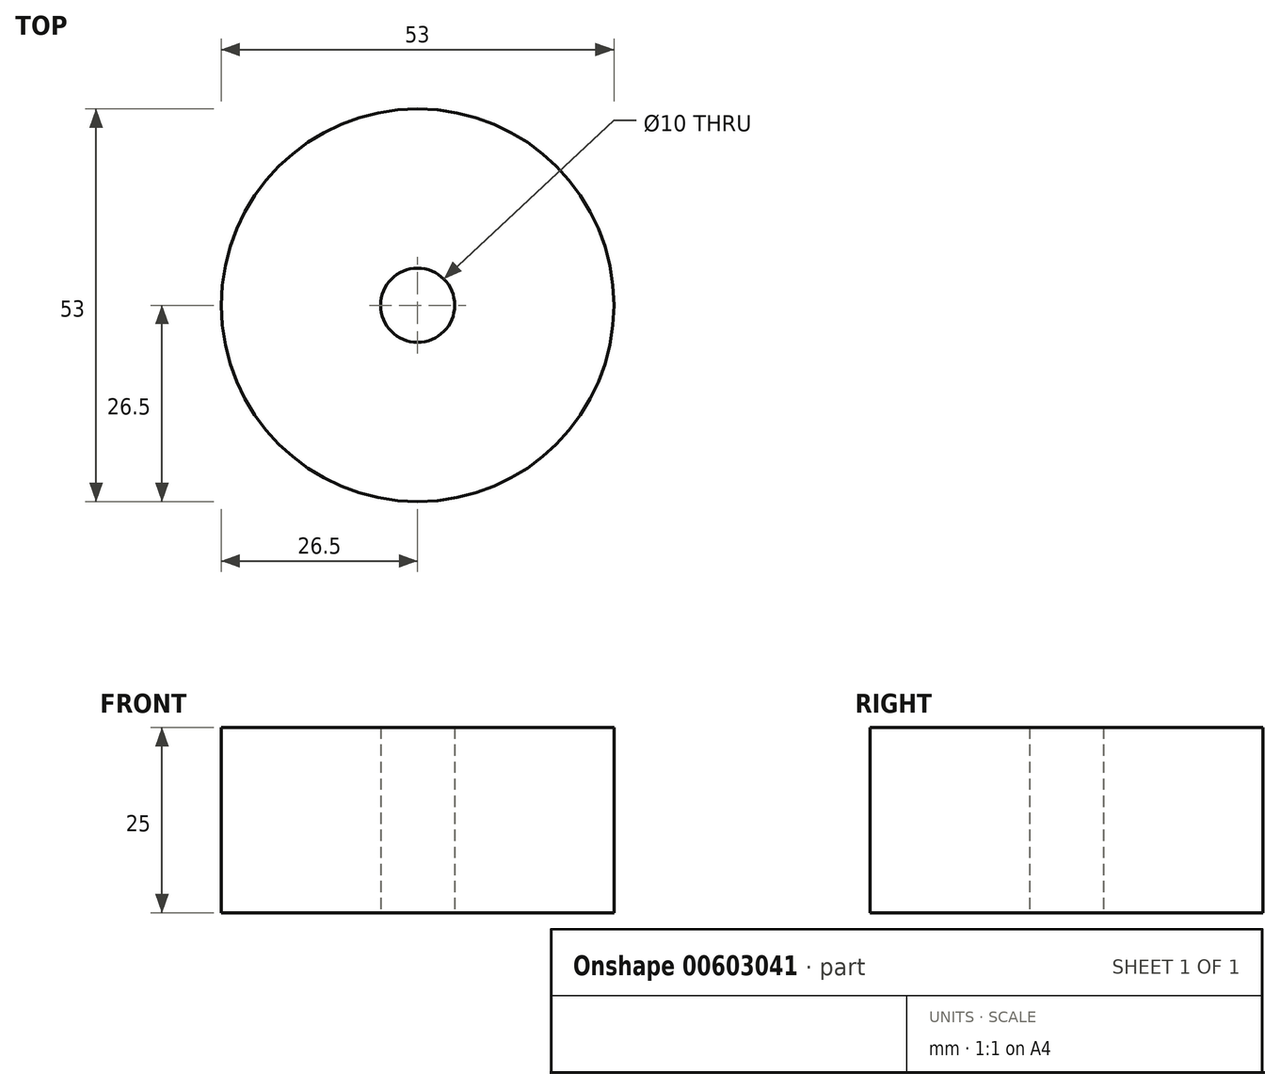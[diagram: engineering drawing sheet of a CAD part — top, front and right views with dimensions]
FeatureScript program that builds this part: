
annotation { "Feature Type Name" : "Feature", "Feature Type Description" : "" }
export const myFeature = defineFeature(function(context is Context, id is Id, definition is map)
    precondition{}
    {
        {
            var Q0;
            Q0=qCreatedBy(makeId("Top.planeOp"),FACE);
            var sketch = newSketch(context, id + "F0", { "sketchPlane" : qUnion([Q0])});
            skCircle(sketch, "E0", {"center": v(0, 0) * mm, "radius": 5 * mm});
            skCircle(sketch, "E1", {"center": v(0, 0) * mm, "radius": 26.5 * mm});
            skSolve(sketch);
        }
        {
            var Q0;
            Q0 = qSketchRegion(id + "F0", true);
            extrude(context, id + "F1", {"entities" : qUnion([Q0]), "depth" : 25 * mm, "offsetDistance" : 25 * mm});
        }
    });
